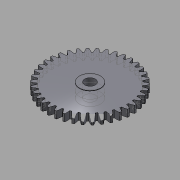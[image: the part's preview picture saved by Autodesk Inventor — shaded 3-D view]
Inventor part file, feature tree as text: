
AUTODESK INVENTOR PART (.ipt)
format: ipt  version: 2015 (Build 190159000, 159)  size: 347,136 bytes
history: native  units: in
note: dims shown in document units (in); Inventor stores cm internally (conversion verified against a paired STEP export)
features: other x13, sketch x5, plane x2
ambient origin geometry x8: Origin, YZ Plane, XZ Plane, XY Plane, X Axis, Y Axis, Z Axis, Center Point
bodies: Solid1 (feature_tree)
feature tree (20):
  other  "Spur Gear28_MIR3.ipt"
  other  "Solid1::Spur Gear28_MIR3.ipt"
  other  "TaggingFeature1"
  sketch  "Sketch1"  dims[d0=0.3937in]
  sketch  "Sketch2"  dims[d16=0.5709in d17=0.0in d41=0.0in d43=0.5709in d46=0.5709in d47=0.0in d48=0.0in]
  sketch  "Sketch3"
  sketch  "Sketch4"
  sketch  "Sketch5"
  plane  "XZ Plane_1"
  plane  "Work Plane2"
  other  "Z Axis_1"
  other  "Srf1"
  other  "Srf1::Derived"
  other  "Distance iMate"
  other  "Align iMate"
  other  "Mesh iMate"
  other  "Axis iMate"
  other  "Position iMate"
  other  "Mesh iMate2"
  other  "Start plane iMate"
